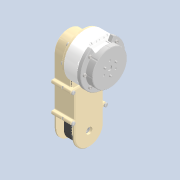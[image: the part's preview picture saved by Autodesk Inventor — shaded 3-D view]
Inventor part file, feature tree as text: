
AUTODESK INVENTOR PART (.ipt)
format: ipt  version: 2020.2 (Build 242310000, 310)  size: 3,809,792 bytes
history: native  units: in
note: dims shown in document units (in); Inventor stores cm internally (conversion verified against a paired STEP export)
features: other x64, extrude x1, sketch x1
ambient origin geometry x8: Origin, YZ Plane, XZ Plane, XY Plane, X Axis, Y Axis, Z Axis, Center Point
bodies: Solid1 (feature_tree)
feature tree (66):
  other  "Ensamble Final.iam"
  other  "Acople Muslo.ipt:1"
  other  "DIN 963 - M4 x 16.ipt:1"
  other  "DIN 963 - M4 x 16.ipt:2"
  other  "DIN 963 - M4 x 16.ipt:3"
  other  "DIN 912 - M4 x 0,7 x 12 x 10,25.ipt:1"
  other  "DIN 912 - M4 x 0,7 x 12 x 10,25.ipt:2"
  other  "DIN 912 - M4 x 0,7 x 12 x 10,25.ipt:3"
  other  "DIN 912 - M4 x 0,7 x 12 x 10,25.ipt:4"
  other  "DIN 912 - M4 x 0,7 x 12 x 10,25.ipt:5"
  other  "DIN 912 - M4 x 0,7 x 12 x 10,25.ipt:6"
  other  "DIN 912 - M4 x 0,7 x 12 x 10,25.ipt:7"
  other  "Cubierta Externa 1.ipt:1"
  other  "Cubierta Externa 2.ipt:1"
  other  "Polea 1.ipt:1"
  other  "DIN 7985 (H) - M4x10-H.ipt:1"
  other  "DIN 7985 (H) - M4x10-H.ipt:2"
  other  "DIN 7985 (H) - M4x10-H.ipt:3"
  other  "DIN 7985 (H) - M4x10-H.ipt:4"
  other  "DIN 125 - A 5,3.ipt:1"
  other  "DIN 125 - A 5,3.ipt:2"
  other  "DIN 125 - A 5,3.ipt:3"
  other  "DIN 7985 (H) - M4x25-H.ipt:1"
  other  "DIN 7985 (H) - M4x25-H.ipt:2"
  other  "DIN 7985 (H) - M4x25-H.ipt:3"
  other  "SKF_W 61801-2RS1.iam:1::SKF_W 61801-2RS1_PART1.ipt:1"
  other  "SKF_W 61801-2RS1.iam:1::SKF_W 61801-2RS1_PART2.ipt:1"
  other  "SKF_W 61801-2RS1.iam:1::SKF_W 61801-2RS1_PART3.ipt:1"
  other  "SKF_W 61801-2RS1.iam:1::SKF_W 61801-2RS1_PART3.ipt:2"
  other  "SKF_W 61801-2RS1.iam:1::SKF_W 61801-2RS1_PART3.ipt:3"
  other  "SKF_W 61801-2RS1.iam:1::SKF_W 61801-2RS1_PART3.ipt:4"
  other  "SKF_W 61801-2RS1.iam:1::SKF_W 61801-2RS1_PART3.ipt:5"
  other  "SKF_W 61801-2RS1.iam:1::SKF_W 61801-2RS1_PART3.ipt:6"
  other  "SKF_W 61801-2RS1.iam:1::SKF_W 61801-2RS1_PART3.ipt:7"
  other  "SKF_W 61801-2RS1.iam:1::SKF_W 61801-2RS1_PART3.ipt:8"
  other  "SKF_W 61801-2RS1.iam:1::SKF_W 61801-2RS1_PART3.ipt:9"
  other  "SKF_W 61801-2RS1.iam:1::SKF_W 61801-2RS1_PART3.ipt:10"
  other  "SKF_W 61801-2RS1.iam:1::SKF_W 61801-2RS1_PART3.ipt:11"
  other  "SKF_W 61801-2RS1.iam:1::SKF_W 61801-2RS1_PART3.ipt:12"
  other  "SKF_W 61801-2RS1.iam:2::SKF_W 61801-2RS1_PART1.ipt:1"
  other  "SKF_W 61801-2RS1.iam:2::SKF_W 61801-2RS1_PART2.ipt:1"
  other  "SKF_W 61801-2RS1.iam:2::SKF_W 61801-2RS1_PART3.ipt:1"
  other  "SKF_W 61801-2RS1.iam:2::SKF_W 61801-2RS1_PART3.ipt:2"
  other  "SKF_W 61801-2RS1.iam:2::SKF_W 61801-2RS1_PART3.ipt:3"
  other  "SKF_W 61801-2RS1.iam:2::SKF_W 61801-2RS1_PART3.ipt:4"
  other  "SKF_W 61801-2RS1.iam:2::SKF_W 61801-2RS1_PART3.ipt:5"
  other  "SKF_W 61801-2RS1.iam:2::SKF_W 61801-2RS1_PART3.ipt:6"
  other  "SKF_W 61801-2RS1.iam:2::SKF_W 61801-2RS1_PART3.ipt:7"
  other  "SKF_W 61801-2RS1.iam:2::SKF_W 61801-2RS1_PART3.ipt:8"
  other  "SKF_W 61801-2RS1.iam:2::SKF_W 61801-2RS1_PART3.ipt:9"
  other  "SKF_W 61801-2RS1.iam:2::SKF_W 61801-2RS1_PART3.ipt:10"
  other  "SKF_W 61801-2RS1.iam:2::SKF_W 61801-2RS1_PART3.ipt:11"
  other  "SKF_W 61801-2RS1.iam:2::SKF_W 61801-2RS1_PART3.ipt:12"
  other  "Ensamble Pierna.Arnés13.iam:1::Ensamble Pierna.Arnés13.ipt:1"
  other  "Motor.ipt:3"
  other  "DIN 7985 (H) - M4x22-H.ipt:1"
  other  "DIN 7985 (H) - M4x22-H.ipt:2"
  other  "DIN 7985 (H) - M4x22-H.ipt:3"
  other  "DIN 7985 (H) - M4x22-H.ipt:4"
  other  "Correa.ipt:1"
  other  "DIN 934 - M4 x 0,7.ipt:1"
  other  "DIN 934 - M4 x 0,7.ipt:2"
  other  "DIN 934 - M4 x 0,7.ipt:3"
  other  "DIN 934 - M4 x 0,7.ipt:4"
  extrude  "Extrusion1"  Depth=0.3937in TaperAngle=0.0deg
  sketch  "Sketch1"  dims[d0=0.3937in d1=0.1in d2=0.0in]
